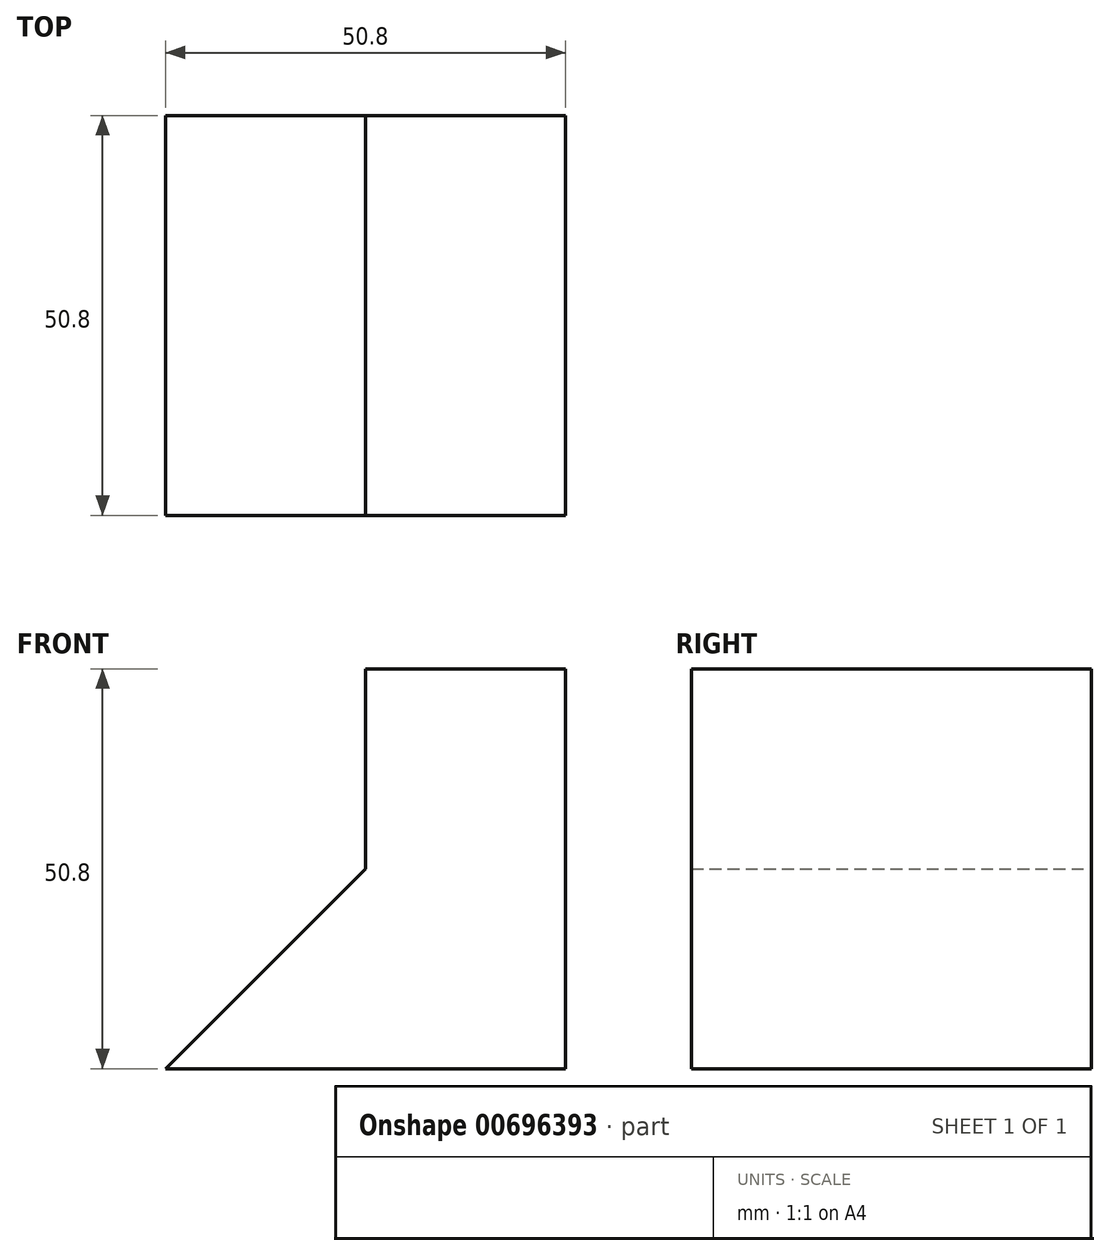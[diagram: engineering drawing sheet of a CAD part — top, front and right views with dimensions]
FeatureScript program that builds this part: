
annotation { "Feature Type Name" : "Feature", "Feature Type Description" : "" }
export const myFeature = defineFeature(function(context is Context, id is Id, definition is map)
    precondition{}
    {
        {
            var Q0;
            Q0=qCreatedBy(makeId("Front.planeOp"),FACE);
            var sketch = newSketch(context, id + "F0", { "sketchPlane" : qUnion([Q0])});
            skLineSegment(sketch, "E0", {"start": v(0, 0) * mm, "end": v(-50.8, 0) * mm});
            skLineSegment(sketch, "E1", {"start": v(0, 0) * mm, "end": v(0, 50.8) * mm});
            skLineSegment(sketch, "E2", {"start": v(0, 50.8) * mm, "end": v(-25.4, 50.8) * mm});
            skLineSegment(sketch, "E3", {"start": v(-25.4, 50.8) * mm, "end": v(-25.4, 25.4) * mm});
            skLineSegment(sketch, "E4", {"start": v(-25.4, 25.4) * mm, "end": v(-50.8, 0) * mm});
            skSolve(sketch);
        }
        {
            var Q0;
            Q0=makeQuery(id+"F0.imprint","IMPRINT",FACE,{"disambiguationData":[TD([[makeQuery(id+"F0.imprint","IMPRINT",EDGE,{"derivedFrom":sQuery(id+"F0.wireOp",EDGE,"E0")}),-1.0]])]});
            extrude(context, id + "F1", {"entities" : qUnion([Q0]), "depth" : 50.8 * mm, "offsetDistance" : 25.4 * mm});
        }
    });
